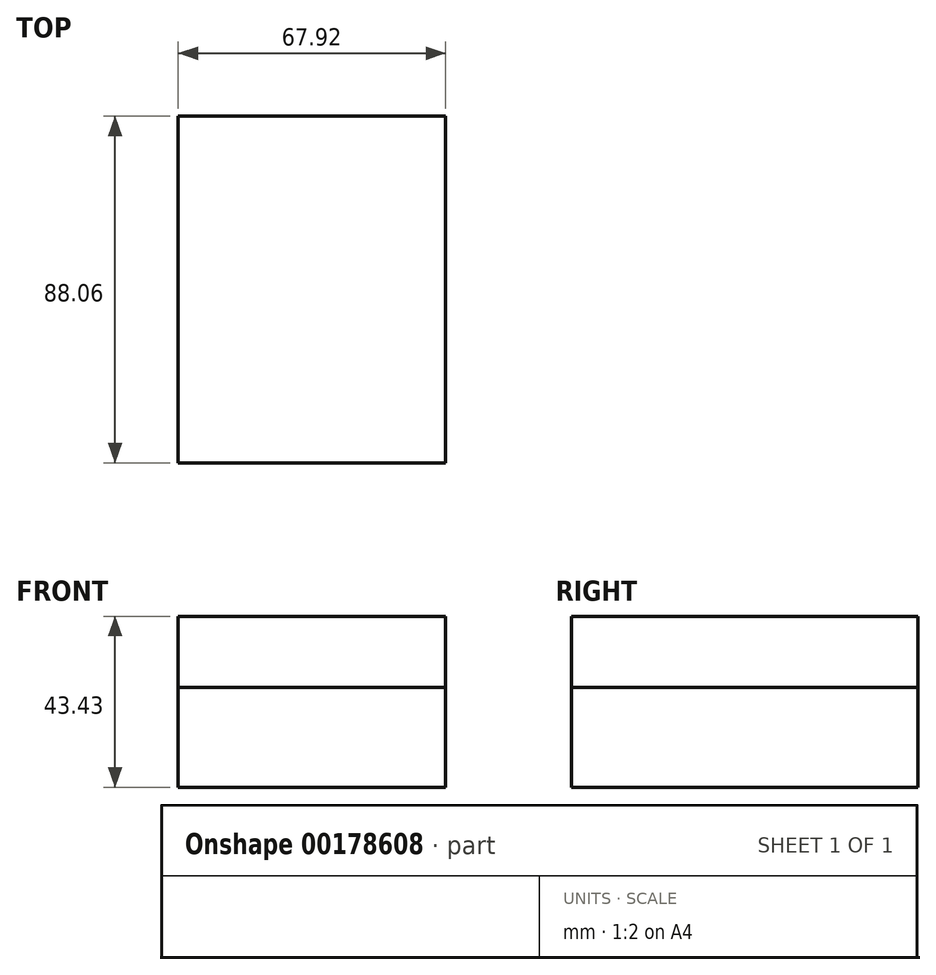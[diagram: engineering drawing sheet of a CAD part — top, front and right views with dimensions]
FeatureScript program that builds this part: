
annotation { "Feature Type Name" : "Feature", "Feature Type Description" : "" }
export const myFeature = defineFeature(function(context is Context, id is Id, definition is map)
    precondition{}
    {
        {
            var Q0;
            Q0=qCreatedBy(makeId("Top.planeOp"),FACE);
            var sketch = newSketch(context, id + "F0", { "sketchPlane" : qUnion([Q0])});
            skLineSegment(sketch, "E0.bottom", {"start": v(33.96, 44.03) * mm, "end": v(-33.96, 44.03) * mm});
            skLineSegment(sketch, "E0.top", {"start": v(33.96, -44.03) * mm, "end": v(-33.96, -44.03) * mm});
            skLineSegment(sketch, "E0.left", {"start": v(33.96, 44.03) * mm, "end": v(33.96, -44.03) * mm});
            skLineSegment(sketch, "E0.right", {"start": v(-33.96, 44.03) * mm, "end": v(-33.96, -44.03) * mm});
            skPoint(sketch, "E0.middle", {"position": v(0, 0) * mm});
            skSolve(sketch);
        }
        {
            var Q0;
            Q0=makeQuery(id+"F0.imprint","IMPRINT",FACE,{"disambiguationData":[TD([[makeQuery(id+"F0.imprint","IMPRINT",EDGE,{"derivedFrom":sQuery(id+"F0.wireOp",EDGE,"E0.bottom")}),1.0]])]});
            extrude(context, id + "F1", {"entities" : qUnion([Q0]), "depth" : 43.43 * mm, "offsetDistance" : 25.4 * mm});
        }
        {
            var Q0;
            Q0=makeQuery(id+"F0.imprint","IMPRINT",FACE,{"disambiguationData":[TD([[makeQuery(id+"F0.imprint","IMPRINT",EDGE,{"derivedFrom":sQuery(id+"F0.wireOp",EDGE,"E0.bottom")}),1.0]])]});
            extrude(context, id + "F2", {"entities" : qUnion([Q0]), "depth" : 25.4 * mm});
        }
    });
